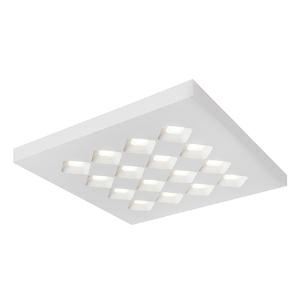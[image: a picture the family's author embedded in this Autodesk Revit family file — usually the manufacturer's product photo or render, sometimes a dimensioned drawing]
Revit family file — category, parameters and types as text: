
# Revit family: 3f_filippi_-_3f_diagon_p_soft_ugr_tunable_white_3f_filippi_-_12142_-_3f_diagon_p_25w_dt8_tw_soft_ugr_596_010de4e3b6c80052
name_source: partatom
category: Lighting Fixtures
units: mm (PartAtom-declared; Revit-internal decimal feet)

## family parameters
Cut with Voids When Loaded = No
Host = Face
Light Source = No
Part Type = Normal
Room Calculation Point = No
Round Connector Dimension = Use Diameter
Shared = No

## types (1)
- 3F Filippi - 3F Dìagon P Soft UGR Tunable White (1 x LED, 3567 lm, 28 W, 6500 K)
    Apparent Load = 28 VA
    Approval mark = ENEC
    CIE Flux Codes = 59 92 100 100 100
    Color Rendering = 80
    Color Temperature = 6500 K
    Control Gear = Electronic transformer
    Default Elevation = 1800 mm
    Description = ILLUMINOTECHNICAL
Luminous efficiency 100% (DLOR 100%, ULOR 0%).
Initial luminous flux of the luminaire 3567 lm.
Direct symmetric distribution.
Installation Interdistance Transv.D = 1.23 x hu - Long.D = 1.23 x hu.
Average luminance <3000 cd/m² for radial angles >65°.
Tabular UGR (CIE 117 - 4H-8H; S=0.25H; 70/50/20): RUG 18.6 - 18.6.
Beam angle: 102° - 101°.
Luminous efficacy 127 lm/W.
Lifetime (L95/B10): 30000 h. (tq+25°C)
Lifetime (L90/B10): 50000 h. (tq+25°C)
Lifetime (L80/B10): 80000 h. (tq+25°C)
Lifetime (L75/B10): 100000 h. (tq+25°C)
Sudden decreased luminous flux after 50000 hours: 0% (C0).
Photobiological safety in compliance with IEC/TR 62778: RG0 risk exempt, (IEC 62471).
In compliance with IEC/EN 62722-2-1 - IEC/EN 62717 standards.

SOURCE
Squared LED module 25W/TW.
Energy efficiency class (UE 2019/2020 - UE 2019/2015): D.
CIE 13.3 Colour rendering index: CRI >80 (R9 <50%).
IES TM-30 Fidelity Index: Rf = 84 Rg = 95.
The colour temperature can be adjusted between 2700 K and 6500 K.
Colour initial tolerance (MacAdam): SDCM 3.

MECHANICAL
White painted frame.
Height only 40 mm.
Housing in hot-galvanised steel, painted in white polyester.
Honeycombed diagonal screen in white anti-glare polycarbonate.
Opal methacrylate (PMMA) rhomboid lenses with differentiated, engraved and prismatic surfaces for diffused, soft lighting and excellent visual comfort.
Luminaire with limited surface temperature. - D - (EN 60598-2-24)
Dimensions: 596x596 mm, height 40 mm. Weight 6.825 kg.
IP40 protection degree.
Mechanical strength to impacts IK06 (1 joule).
Glow-wire test resistance 650°C.

ELECTRICAL
Halogen Free DALI DT8, PUSH-DIM, electronic wiring 230V-50/60Hz, power factor 0.90 at full load, THD <25%, constant output current, class I, 1 driver, 1 DALI addresse.
Power of the luminaire 28 W.
CE - IEC 60598-1 - EN 60598-1.
SAFE FLICKER: PstLM=<1 and SVM=<0.4 (IEC TR 61547-1 and IEC TR 63158), to ensure a more comfortable and safe light.
Luminaire compliant with EN 60598-2-22 for power supply from a centralised emergency system CPSS (Central Power Supply System), not incorporated in the luminaire - high risk areas excluded. The default power and flux are 100% in AC and 15% in DC.
Ambient temperature from 0°C to +25°C.
Temperature class T6 max 85°C.
5-pole terminal block (L-N-PE-DA/DA) quick connection for line connection with connection capacity 2x2.5 mm² per poles.
Relative humidity UR: <85%.

INSTALLATION
Ceiling.

APPLICATIONS
Any environments requiring light which aims for the wellness of people.
Environments: staterooms, with VDTs, offices.
Environments with exacting visual tasks, where diffused soft light for optimum visual comfort is required.

LIGHT MANAGEMENT
Recommended minimum setting: 10%.
The luminaire, equipped with DALI DT8 driver, is designed for adjusting the luminous flux and colour temperature; can be controlled manually or automatically/manually with 3F HCL technology or 3F Bluetooth.

WARNING
Luminaire designed for disposal/recycling at end-of-life.
Replaceable (LED only) light source by a professional. Replaceable control gear by a professional.
    Height = 40 mm  [stored 0.131234 ft]
    Lamp = 1 x LED
    Lamp Light Flux = 3567 lm
    Lamp Power = 28 W
    Lamp count = 1
    Length = 596 mm
    Lifetime = 50000 h
    Luminous efficacy = 127 lm/W
    Manufacturer = 3F Filippi
    ModVariant = No
    Model = 3F Filippi - 12142 - 3F Diagon P 25W DT8 TW SOFT UGR 596x596 (CCT 6500)
    Mounting Place = Ceiling
    Mounting Type = Surface mounted
    Number of Poles = 1
    OnlyDefault = Yes
    Power Factor = 1
    Product Name = 3F Filippi - 3F Dìagon P Soft UGR Tunable White
    Product group = ceiling mounted luminaire
    ProductGroupID = 3
    Protection Class = Protection class I
    Protection Degree = IP 40
    RLX_Detail_Level = 1
    RLX_Emergency_Light_Flux = 0 lm
    RLX_Emergency_Type = 0
    RLX_Emergency_Type_DB = No
    RlxData = <blob elided: 96953 chars, md5=746744a8>
    Socket = socket
    Standby Power = 0 W
    System Light Flux = 3567 lm
    System Power = 28 W
    Type Comments = Product without accessories
    Type Image = 3ffilippi_3f_diagon_p_soft_ugr_tunable_white.jpg
    URL = http://relux.com
    VarID = ---
    Voltage = 0 V
    Weight = 0.00 kg
    Width = 596 mm

note: [stored X ft] marks values corroborated as IEEE doubles in the binary element streams (Revit-internal decimal feet)

## geometry (parser evidence)
native form markers: Blend x4, Sweep x11
no freeform markers — native parametric forms only
